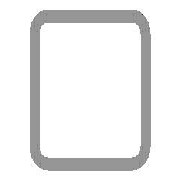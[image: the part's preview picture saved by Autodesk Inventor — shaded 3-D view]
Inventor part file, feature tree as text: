
AUTODESK INVENTOR PART (.ipt)
format: ipt  version: 2011 (Build 150239000, 239)  size: 126,464 bytes
history: native  units: mm (DEFAULTED — no unit token found)
features: other x4, sketch x2, plane x1
ambient origin geometry x8: Origin, YZ Plane, XZ Plane, XY Plane, X Axis, Y Axis, Z Axis, Center Point
bodies: Solid1 (feature_tree), Body (feature_tree)
feature tree (7):
  parser-record x1  (decoder bookkeeping rows leaked as tree rows — omitted from the tree; the rows remain in map.json)
  other  "Driven Length"
  other  "Start plane"
  other  "End plane"
  sketch  "Sketch3"  dims[d3=177.8mm]
  plane  "Work Plane3"
  sketch  "Sketch4"  dims[d4=0.0mm d7=3.75mm d10=25.0mm d11=25.0mm d12=2.5mm d13=-0.0mm d14=177.8mm d15=12.5mm d16=12.5mm d17=90.0deg d18=177.8mm]
